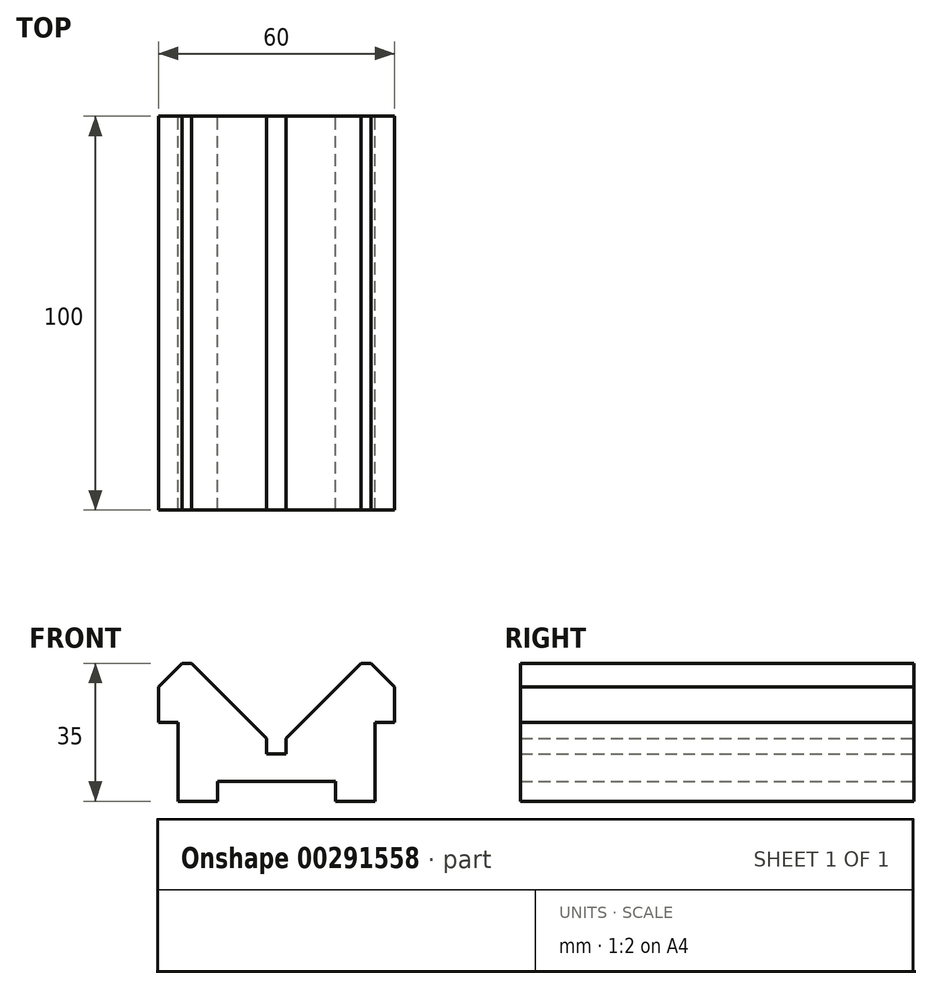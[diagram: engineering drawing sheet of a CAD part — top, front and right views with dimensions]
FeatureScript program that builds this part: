
annotation { "Feature Type Name" : "Feature", "Feature Type Description" : "" }
export const myFeature = defineFeature(function(context is Context, id is Id, definition is map)
    precondition{}
    {
        {
            var Q0;
            Q0=qCreatedBy(makeId("Front.planeOp"),FACE);
            var sketch = newSketch(context, id + "F0", { "sketchPlane" : qUnion([Q0])});
            skLineSegment(sketch, "E0", {"start": v(0, 0) * mm, "end": v(0, 20) * mm});
            skLineSegment(sketch, "E1", {"start": v(0, 20) * mm, "end": v(-5, 20) * mm});
            skLineSegment(sketch, "E2", {"start": v(-5, 20) * mm, "end": v(-5, 29) * mm});
            skLineSegment(sketch, "E3", {"start": v(-5, 29) * mm, "end": v(1, 35) * mm});
            skLineSegment(sketch, "E4", {"start": v(1, 35) * mm, "end": v(3.5, 35) * mm});
            skLineSegment(sketch, "E5", {"start": v(3.5, 35) * mm, "end": v(22.5, 16) * mm});
            skLineSegment(sketch, "E6", {"start": v(22.5, 16) * mm, "end": v(22.5, 12) * mm});
            skLineSegment(sketch, "E7", {"start": v(22.5, 12) * mm, "end": v(27.5, 12) * mm});
            skLineSegment(sketch, "E8", {"start": v(27.5, 12) * mm, "end": v(27.5, 16) * mm});
            skLineSegment(sketch, "E9", {"start": v(27.5, 16) * mm, "end": v(46.5, 35) * mm});
            skLineSegment(sketch, "E10", {"start": v(46.5, 35) * mm, "end": v(49, 35) * mm});
            skLineSegment(sketch, "E11", {"start": v(49, 35) * mm, "end": v(55, 29) * mm});
            skLineSegment(sketch, "E12", {"start": v(55, 29) * mm, "end": v(55, 20) * mm});
            skLineSegment(sketch, "E13", {"start": v(55, 20) * mm, "end": v(50, 20) * mm});
            skLineSegment(sketch, "E14", {"start": v(50, 20) * mm, "end": v(50, 0) * mm});
            skLineSegment(sketch, "E15", {"start": v(50, 0) * mm, "end": v(40, 0) * mm});
            skLineSegment(sketch, "E16", {"start": v(40, 0) * mm, "end": v(40, 5) * mm});
            skLineSegment(sketch, "E17", {"start": v(40, 5) * mm, "end": v(10, 5) * mm});
            skLineSegment(sketch, "E18", {"start": v(10, 5) * mm, "end": v(10, 0) * mm});
            skLineSegment(sketch, "E19", {"start": v(10, 0) * mm, "end": v(0, 0) * mm});
            skSolve(sketch);
        }
        {
            var Q0;
            Q0 = qSketchRegion(id + "F0", true);
            extrude(context, id + "F1", {"entities" : qUnion([Q0]), "depth" : 100 * mm});
        }
    });
